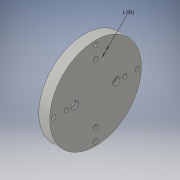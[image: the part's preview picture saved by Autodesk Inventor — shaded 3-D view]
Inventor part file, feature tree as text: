
AUTODESK INVENTOR PART (.ipt)
format: ipt  version: 2016 (Build 200138000, 138)  size: 173,568 bytes
history: native  units: in
note: dims shown in document units (in); Inventor stores cm internally (conversion verified against a paired STEP export)
features: sketch x6, extrude x3, revolve x1
ambient origin geometry x8: Origin, YZ Plane, XZ Plane, XY Plane, X Axis, Y Axis, Z Axis, Center Point
bodies: Solid1 (feature_tree)
feature tree (10):
  revolve  "Revolution1"  [1 undecoded]
  extrude  "Extrusion1"  Depth=0.105in
  sketch  "Sketch3"  dims[d4=0.105in d5=0.255in]
  sketch  "Sketch4"  dims[d6=0.2in d7=0.1in]
  extrude  "Extrusion2"  Depth=0.105in
  sketch  "Sketch5"  dims[d8=90.0deg]
  extrude  "Extrusion4"  Depth=0.1in
  sketch  "Sketch1"  dims[d0=1.2499in d1=0.3in]
  sketch  "Sketch2"  dims[d2=0.22in d3=0.105in]
  sketch  "Sketch8"  dims[d9=0.1181in d10=1.5748in d12=360.0deg d14=0.5in d15=0.0in d16=0.255in d17=0.1275in d18=0.1181in d19=1.5748in d21=360.0deg d23=0.2in d24=0.0in d25=1.14in d26=0.787in d42=1.0in d43=0.0in]
note: 1 required parameter value undecoded (feature->parameter linkage not recoverable at this tier; creation-order binding heuristic only, values carry confidence <= 0.55)
